# Revit family: BIMLIB_КронштейнКрепежный_GRANDLINE
name_source: partatom
category: Обобщенные модели
revit_build: Autodesk Revit 2017 (Build: 20170118_1100(x64)
units: mm (PartAtom-declared; Revit-internal decimal feet)

## family parameters
Всегда вертикально = Нет
Может служить основой для арматурных стержней = Нет
На основе рабочей плоскости = Да
Общий = Нет
При загрузке вырезать с полостями = Нет
Размер круглого соединителя = Использовать диаметр
Тип детали = Нормальный
Точка расчета площади = Нет

## types (8) — shared parameters
ADSK_URL документации изделия = https://www.grandline.ru
ADSK_URL страницы изделия = https://www.grandline.ru
ADSK_Версия Revit = 2017
ADSK_Группирование = Доборные элементы
ADSK_Единица измерения = шт
ADSK_Завод-изготовитель = Grand Line
ADSK_Материал = GL_Сталь
ADSK_Размер_Толщина = 2 мм
ADSK_Размер_Ширина = 50 мм
BL_BIM library = https://bimlib.pro
URL = https://www.grandline.ru
Анкер_Длина = 80 мм
Изготовитель = Grand Line
Отметка по умолчанию = 1219 мм
zero-valued in all types: ADSK_Масса, ADSK_Материал тип подсчета

## per-type parameters (varying)
| type | ADSK_Наименование | ADSK_Размер_Длина | Описание |
| 50х50х50 | Крепежный кронштейн 50х50х50 | 50 мм | Крепежный кронштейн 50х50х50 |
| 50х50х90 | Крепежный кронштейн 50х50х90 | 90 мм | Крепежный кронштейн 50х50х90 |
| 50х50х100 | Крепежный кронштейн 50х50х100 | 100 мм | Крепежный кронштейн 50х50х100 |
| 50х50х150 | Крепежный кронштейн 50х50х150 | 150 мм | Крепежный кронштейн 50х50х150 |
| 50х50х180 | Крепежный кронштейн 50х50х180 | 180 мм | Крепежный кронштейн 50х50х180 |
| 50х50х200 | Крепежный кронштейн 50х50х200 | 200 мм | Крепежный кронштейн 50х50х200 |
| 50х50х250 | Крепежный кронштейн 50х50х250 | 250 мм | Крепежный кронштейн 50х50х250 |
| 50х50х120 | Крепежный кронштейн 50х50х120 | 120 мм | Крепежный кронштейн 50х50х120 |
